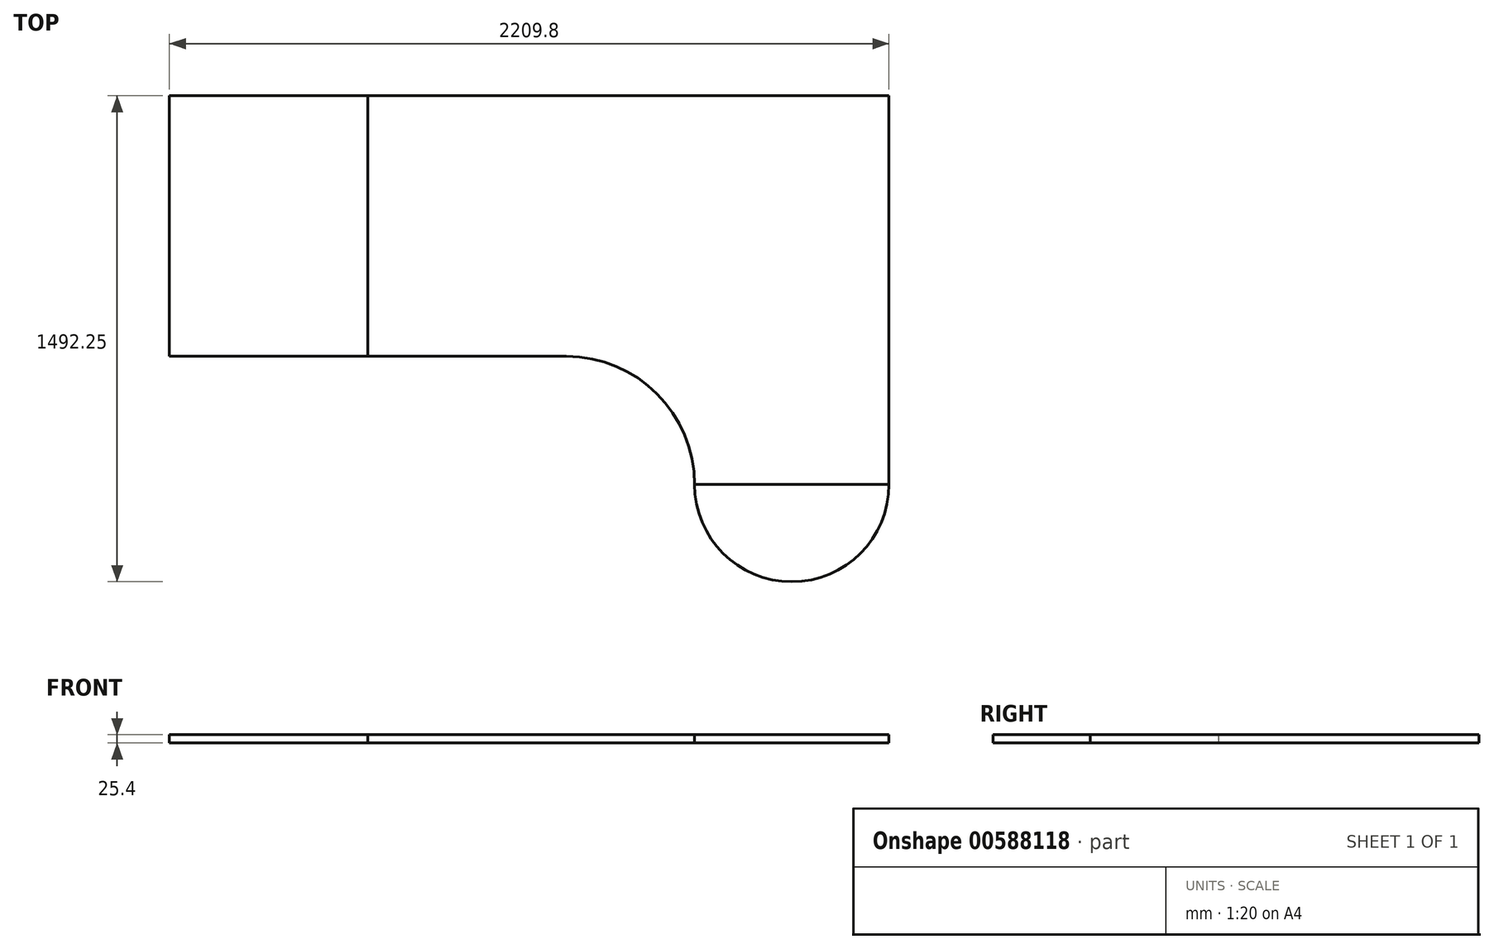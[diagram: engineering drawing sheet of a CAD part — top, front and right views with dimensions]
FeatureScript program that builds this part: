
annotation { "Feature Type Name" : "Feature", "Feature Type Description" : "" }
export const myFeature = defineFeature(function(context is Context, id is Id, definition is map)
    precondition{}
    {
        {
            var Q0;
            Q0=qCreatedBy(makeId("Top.planeOp"),FACE);
            var sketch = newSketch(context, id + "F0", { "sketchPlane" : qUnion([Q0])});
            skLineSegment(sketch, "E0.bottom", {"start": v(-609.6, 0) * mm, "end": v(0, 0) * mm});
            skLineSegment(sketch, "E0.top", {"start": v(-609.6, 800.1) * mm, "end": v(0, 800.1) * mm});
            skLineSegment(sketch, "E0.left", {"start": v(0, 0) * mm, "end": v(0, 800.1) * mm});
            skLineSegment(sketch, "E0.right", {"start": v(-609.6, 0) * mm, "end": v(-609.6, 800.1) * mm});
            skSolve(sketch);
        }
        {
            var Q0;
            Q0=makeQuery(id+"F0.imprint","IMPRINT",FACE,{"disambiguationData":[TD([[makeQuery(id+"F0.imprint","IMPRINT",EDGE,{"derivedFrom":sQuery(id+"F0.wireOp",EDGE,"E0.bottom")}),1.0]])]});
            extrude(context, id + "F1", {"entities" : qUnion([Q0]), "depth" : 25.4 * mm, "offsetDistance" : 25.4 * mm});
        }
        {
            var Q0;
            Q0=qCreatedBy(makeId("Top.planeOp"),FACE);
            var sketch = newSketch(context, id + "F2", { "sketchPlane" : qUnion([Q0])});
            skLineSegment(sketch, "E1", {"start": v(0, 800.1) * mm, "end": v(1600.2, 800.1) * mm});
            skLineSegment(sketch, "E2", {"start": v(1600.2, 800.1) * mm, "end": v(1600.2, -393.7) * mm});
            skLineSegment(sketch, "E3", {"start": v(1600.2, -393.7) * mm, "end": v(1003.3, -393.7) * mm});
            skLineSegment(sketch, "E4", {"start": v(0, 800.1) * mm, "end": v(0, 0) * mm});
            skLineSegment(sketch, "E5", {"start": v(0, 0) * mm, "end": v(609.6, 0) * mm});
            skArc(sketch, "E6", {"start": v(609.6, 0) * mm, "mid": v(887.99, -115.31) * mm, "end": v(1003.3, -393.7) * mm});
            skSolve(sketch);
        }
        {
            var Q0;
            Q0 = qSketchRegion(id + "F2", true);
            extrude(context, id + "F3", {"entities" : qUnion([Q0]), "depth" : 25.4 * mm, "offsetDistance" : 25.4 * mm});
        }
        {
            var Q0;
            Q0=qCreatedBy(makeId("Top.planeOp"),FACE);
            var sketch = newSketch(context, id + "F4", { "sketchPlane" : qUnion([Q0])});
            skLineSegment(sketch, "E7", {"start": v(1600.2, -393.7) * mm, "end": v(1003.3, -393.7) * mm});
            skArc(sketch, "E8", {"start": v(1600.2, -393.7) * mm, "mid": v(1301.75, -692.15) * mm, "end": v(1003.3, -393.7) * mm});
            skSolve(sketch);
        }
        {
            var Q0;
            Q0 = qSketchRegion(id + "F4", true);
            extrude(context, id + "F5", {"entities" : qUnion([Q0]), "depth" : 25.4 * mm, "offsetDistance" : 25.4 * mm});
        }
    });
